# Revit family: O3IP_14BF
name_source: partatom
category: Mechanical Equipment
units: mm (PartAtom-declared; Revit-internal decimal feet)

## family parameters
Always vertical = Yes
Cut with Voids When Loaded = No
OmniClass Number = 23.40.40.11.17
OmniClass Title = Refrigerated Cases
Part Type = Normal
Room Calculation Point = No
Round Connector Dimension = Use Radius
Shared = No
Work Plane-Based = Yes

## types (8) — shared parameters
ANTI SWEAT HEATER AMPS = 1 A
BASE HEIGHT = 14 3/4"
BTU ADD PER SHELF PER FOOT = 80
BTU PER FOOT CONVENTIONAL = 1045
BTU PER FOOT PARALLEL = 946
CERTIFICATIONS = NSF 7, UL471, CSA
COIL REFRIGERATION CHARGE = 0.00 lb
CONTROL TYPE = T-STAT
DATE = 05/22/12
DEDICATED CIRCUIT = YES
DEFROST PHASE = 1
DEFROST TIME AND DURATION = 2 @ 60 MIN
DEFROST WATTAGE = 0 W
DIEBOARD HEIGHT = 0"
DISCHARGE AIR TEMPERATURE = 34 °F
DRAIN LINE CONNECTION = Drain Connection
DRAIN LINE DIAMETER = 2"
DRAIN LINE RADIUS = 1"
DRAIN PIPE LENGTH = 0"
DRAIN PIPE TYPE = PVC
DRIP PAN PLUMB TYPE = HARD
Default Elevation = 48"
Description = Wide Multi-Deck Island Merchandiser
ELECTRIC DEFROST = No
ELECTRICAL DEFROST VOLTAGE = 0 V
EQUIPMENT MARK = O3IP
EVAPORATOR TEMPERATURE = 22 °F
FAN AMPS = 1 A
FAN CONNECTOR DESCRIPTION = FAN AND ANTI SWEAT CONNECTOR
FAN NUMBER OF POLES = 1
FAN TYPE = ECM
GROUND FAULT PROTECTION = NO
HEIGHT = 55 1/8"
HOT GAS DEFROST = No
ISOLATED GROUND REQUIRED = NO
Keynote = Deli / Meat
LED LIGHTING BTU ADD PER ROW = 36
LIGHT TYPE = T8 FLUORESCENT
LIGHTING CONNECTION DESCRIPTION = LIGHTING CONNECTOR
LIGHTING NUMBER OF POLES = 1
LIQUID LINE CONNECTION = LIQUID LINE CONNECTION
LIQUID LINE DIAMETER = 0"
LIQUID LINE RADIUS = 0"
Manufacturer = HILL PHOENIX
NUMBER OF WIRES = 3
PHASE = 1
POWER FACTOR = 1
PRESSURE REGULATOR = 0.00 psi
RECEPTICAL MOUNTING HEIGHT ABOVE FLOOR = 19 3/4"
REF PLANE FRONT BACK = 39 15/16"
REVERSE AIR DEFROST = No
SET BACK MODE FOR ENERGY CONSERVATION = NO
SIZE OF COLD WATER HOOK UP = 0"
SIZE OF HOT WATER HOOK-UP = 0"
SUCTION LINE CONNECTION = SUCTION LINE CONNECTION
SUCTION LINE DIAMETER = 1"
SUCTION LINE RADIUS = 0"
T8 LIGHT OR LED LIGHT = Yes
T8 LIGHTING AMPS PER ROW = 1 A
T8 LIGHTING BTU ADD PER ROW = 80
TIME OFF DEFROST = Yes
TOEKICK HEIGHT = 5 1/2"
TOEKICK INSET = 1 1/2"
URL = http://www.hillphoenix.com
VOLTAGE = 120 V
WATER LINE MOUNTING HEIGHT ABOVE FLOOR = 0"
WEIGHT = 0.00 lb
WIDTH = 79 7/8"
zero-valued in all types: CORNICE AND NOSE LIGHT ROWS

## per-type parameters (varying)
- O3IP-8' TOP SILL SD: ANTI SWEAT APPARENT LOAD=98 VA; ANTI SWEAT HEATER WATTAGE=98 W; BTU ADD FOR LIGHTS=2880; CONVENTIONAL EVAPORATOR LOAD=12285; DEFROST AMPS=4 A; FAN AND ANTI SWEAT HEATER APPARENT LOAD=206 VA; FAN APPARENT LOAD=108 VA; FAN QUANTITY=6; FAN WATTAGE=66 W; LED LIGHTING AMPS=1 A; LED LIGHTING AMPS PER ROW=0 A; LED LIGHTING WATTAGE=144 W; LEGEND NUMBER=O3IP-8'; LENGTH=105 5/8"; LENGTH FOR BTU=9; LIGHT AMPS=2 A; LIGHTING APPARENT LOAD=288 VA; LIGHTING WATTAGE=288 VA; Model=O3IP-8'; PARALLEL EVAPORATOR LOAD=11394; REF PLANE LEFT RIGHT=52 13/16"; SHELF LIGHT ROWS=4; T8 LIGHTING AMPS=2 A; T8 LIGHTING WATTAGE=288 W; TOTAL APPARENT FAN-LIGHT AND A/S LOAD=452 VA; TOTAL CASE AMPS=4 A; TOTAL CASE WATTAGE=452 W
- O3IP-12' TOP SILL SD: ANTI SWEAT APPARENT LOAD=130 VA; ANTI SWEAT HEATER WATTAGE=130 W; BTU ADD FOR LIGHTS=6240; CONVENTIONAL EVAPORATOR LOAD=19825; DEFROST AMPS=7 A; FAN AND ANTI SWEAT HEATER APPARENT LOAD=274 VA; FAN APPARENT LOAD=144 VA; FAN QUANTITY=8; FAN WATTAGE=88 W; LED LIGHTING AMPS=3 A; LED LIGHTING AMPS PER ROW=1 A; LED LIGHTING WATTAGE=360 W; LEGEND NUMBER=O3IP-12'; LENGTH=153 5/8"; LENGTH FOR BTU=13; LIGHT AMPS=7 A; LIGHTING APPARENT LOAD=842 VA; LIGHTING WATTAGE=842 VA; Model=O3IP-12'; PARALLEL EVAPORATOR LOAD=18538; REF PLANE LEFT RIGHT=76 13/16"; SHELF LIGHT ROWS=6; T8 LIGHTING AMPS=7 A; T8 LIGHTING WATTAGE=842 W; TOTAL APPARENT FAN-LIGHT AND A/S LOAD=1060 VA; TOTAL CASE AMPS=9 A; TOTAL CASE WATTAGE=1060 W
- O3IP-12', 12" SD: ANTI SWEAT APPARENT LOAD=130 VA; ANTI SWEAT HEATER WATTAGE=130 W; BTU ADD FOR LIGHTS=6240; CONVENTIONAL EVAPORATOR LOAD=19825; DEFROST AMPS=7 A; FAN AND ANTI SWEAT HEATER APPARENT LOAD=274 VA; FAN APPARENT LOAD=144 VA; FAN QUANTITY=8; FAN WATTAGE=88 W; LED LIGHTING AMPS=3 A; LED LIGHTING AMPS PER ROW=1 A; LED LIGHTING WATTAGE=360 W; LEGEND NUMBER=O3IP-12'; LENGTH=153 5/8"; LENGTH FOR BTU=13; LIGHT AMPS=7 A; LIGHTING APPARENT LOAD=842 VA; LIGHTING WATTAGE=842 VA; Model=O3IP-12'; PARALLEL EVAPORATOR LOAD=18538; REF PLANE LEFT RIGHT=76 13/16"; SHELF LIGHT ROWS=6; T8 LIGHTING AMPS=7 A; T8 LIGHTING WATTAGE=842 W; TOTAL APPARENT FAN-LIGHT AND A/S LOAD=1060 VA; TOTAL CASE AMPS=9 A; TOTAL CASE WATTAGE=1060 W
- O3IP-12', 16" SD: ANTI SWEAT APPARENT LOAD=130 VA; ANTI SWEAT HEATER WATTAGE=130 W; BTU ADD FOR LIGHTS=6240; CONVENTIONAL EVAPORATOR LOAD=19825; DEFROST AMPS=7 A; FAN AND ANTI SWEAT HEATER APPARENT LOAD=274 VA; FAN APPARENT LOAD=144 VA; FAN QUANTITY=8; FAN WATTAGE=88 W; LED LIGHTING AMPS=3 A; LED LIGHTING AMPS PER ROW=1 A; LED LIGHTING WATTAGE=360 W; LEGEND NUMBER=O3IP-12'; LENGTH=153 5/8"; LENGTH FOR BTU=13; LIGHT AMPS=7 A; LIGHTING APPARENT LOAD=842 VA; LIGHTING WATTAGE=842 VA; Model=O3IP-12'; PARALLEL EVAPORATOR LOAD=18538; REF PLANE LEFT RIGHT=76 13/16"; SHELF LIGHT ROWS=6; T8 LIGHTING AMPS=7 A; T8 LIGHTING WATTAGE=842 W; TOTAL APPARENT FAN-LIGHT AND A/S LOAD=1060 VA; TOTAL CASE AMPS=9 A; TOTAL CASE WATTAGE=1060 W
- O3IP-8', 12" SD: ANTI SWEAT APPARENT LOAD=98 VA; ANTI SWEAT HEATER WATTAGE=98 W; BTU ADD FOR LIGHTS=2880; CONVENTIONAL EVAPORATOR LOAD=12285; DEFROST AMPS=4 A; FAN AND ANTI SWEAT HEATER APPARENT LOAD=206 VA; FAN APPARENT LOAD=108 VA; FAN QUANTITY=6; FAN WATTAGE=66 W; LED LIGHTING AMPS=1 A; LED LIGHTING AMPS PER ROW=0 A; LED LIGHTING WATTAGE=144 W; LEGEND NUMBER=O3IP-8'; LENGTH=105 5/8"; LENGTH FOR BTU=9; LIGHT AMPS=2 A; LIGHTING APPARENT LOAD=288 VA; LIGHTING WATTAGE=288 VA; Model=O3IP-8'; PARALLEL EVAPORATOR LOAD=11394; REF PLANE LEFT RIGHT=52 13/16"; SHELF LIGHT ROWS=4; T8 LIGHTING AMPS=2 A; T8 LIGHTING WATTAGE=288 W; TOTAL APPARENT FAN-LIGHT AND A/S LOAD=452 VA; TOTAL CASE AMPS=4 A; TOTAL CASE WATTAGE=452 W
- O3IP-8', 16" SD: ANTI SWEAT APPARENT LOAD=98 VA; ANTI SWEAT HEATER WATTAGE=98 W; BTU ADD FOR LIGHTS=2880; CONVENTIONAL EVAPORATOR LOAD=12285; DEFROST AMPS=4 A; FAN AND ANTI SWEAT HEATER APPARENT LOAD=206 VA; FAN APPARENT LOAD=108 VA; FAN QUANTITY=6; FAN WATTAGE=66 W; LED LIGHTING AMPS=1 A; LED LIGHTING AMPS PER ROW=0 A; LED LIGHTING WATTAGE=144 W; LEGEND NUMBER=O3IP-8'; LENGTH=105 5/8"; LENGTH FOR BTU=9; LIGHT AMPS=2 A; LIGHTING APPARENT LOAD=288 VA; LIGHTING WATTAGE=288 VA; Model=O3IP-8'; PARALLEL EVAPORATOR LOAD=11394; REF PLANE LEFT RIGHT=52 13/16"; SHELF LIGHT ROWS=4; T8 LIGHTING AMPS=2 A; T8 LIGHTING WATTAGE=288 W; TOTAL APPARENT FAN-LIGHT AND A/S LOAD=452 VA; TOTAL CASE AMPS=4 A; TOTAL CASE WATTAGE=452 W
- O3IP-12': ANTI SWEAT APPARENT LOAD=130 VA; ANTI SWEAT HEATER WATTAGE=130 W; BTU ADD FOR LIGHTS=6240; CONVENTIONAL EVAPORATOR LOAD=19825; DEFROST AMPS=7 A; FAN AND ANTI SWEAT HEATER APPARENT LOAD=274 VA; FAN APPARENT LOAD=144 VA; FAN QUANTITY=8; FAN WATTAGE=88 W; LED LIGHTING AMPS=3 A; LED LIGHTING AMPS PER ROW=1 A; LED LIGHTING WATTAGE=360 W; LEGEND NUMBER=O3IP-12'; LENGTH=153 5/8"; LENGTH FOR BTU=13; LIGHT AMPS=7 A; LIGHTING APPARENT LOAD=842 VA; LIGHTING WATTAGE=842 VA; Model=O3IP-12'; PARALLEL EVAPORATOR LOAD=18538; REF PLANE LEFT RIGHT=76 13/16"; SHELF LIGHT ROWS=6; T8 LIGHTING AMPS=7 A; T8 LIGHTING WATTAGE=842 W; TOTAL APPARENT FAN-LIGHT AND A/S LOAD=1060 VA; TOTAL CASE AMPS=9 A; TOTAL CASE WATTAGE=1060 W
- O3IP-8': ANTI SWEAT APPARENT LOAD=98 VA; ANTI SWEAT HEATER WATTAGE=98 W; BTU ADD FOR LIGHTS=2880; CONVENTIONAL EVAPORATOR LOAD=12285; DEFROST AMPS=4 A; FAN AND ANTI SWEAT HEATER APPARENT LOAD=206 VA; FAN APPARENT LOAD=108 VA; FAN QUANTITY=6; FAN WATTAGE=66 W; LED LIGHTING AMPS=1 A; LED LIGHTING AMPS PER ROW=0 A; LED LIGHTING WATTAGE=144 W; LEGEND NUMBER=O3IP-8'; LENGTH=105 5/8"; LENGTH FOR BTU=9; LIGHT AMPS=2 A; LIGHTING APPARENT LOAD=288 VA; LIGHTING WATTAGE=288 VA; Model=O3IP-8'; PARALLEL EVAPORATOR LOAD=11394; REF PLANE LEFT RIGHT=52 13/16"; SHELF LIGHT ROWS=4; T8 LIGHTING AMPS=2 A; T8 LIGHTING WATTAGE=288 W; TOTAL APPARENT FAN-LIGHT AND A/S LOAD=452 VA; TOTAL CASE AMPS=4 A; TOTAL CASE WATTAGE=452 W

## geometry (parser evidence)
native form markers: Blend x2, Sweep x6
no freeform markers — native parametric forms only
